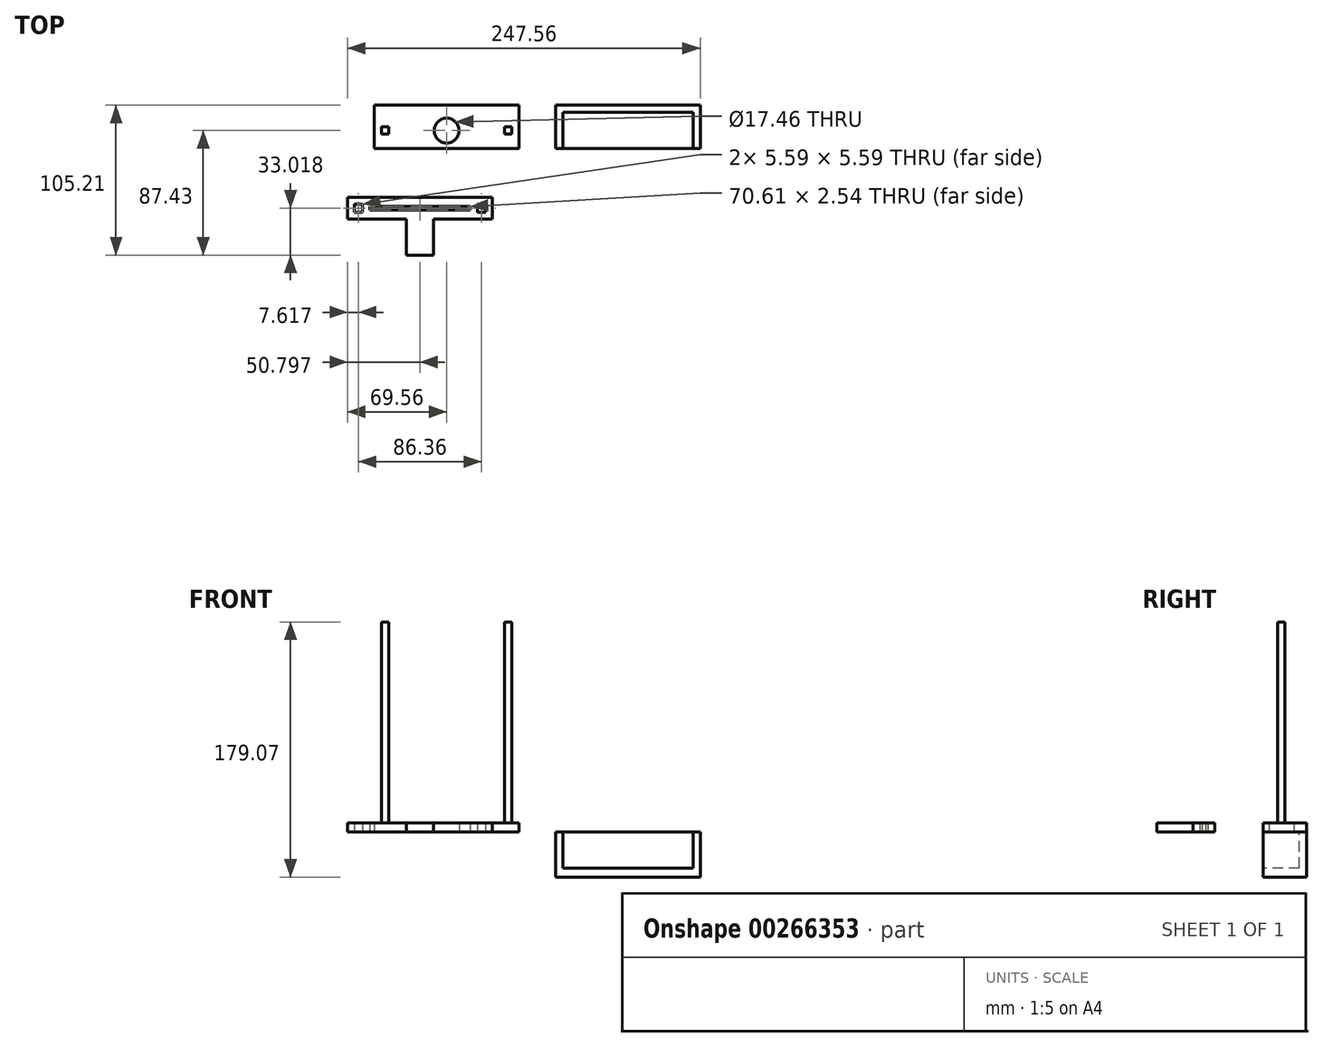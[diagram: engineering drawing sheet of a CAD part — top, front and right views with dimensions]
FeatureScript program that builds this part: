
annotation { "Feature Type Name" : "Feature", "Feature Type Description" : "" }
export const myFeature = defineFeature(function(context is Context, id is Id, definition is map)
    precondition{}
    {
        {
            var Q0;
            Q0=qCreatedBy(makeId("Top.planeOp"),FACE);
            var sketch = newSketch(context, id + "F0", { "sketchPlane" : qUnion([Q0])});
            skLineSegment(sketch, "E0.bottom", {"start": v(45.72, 12.7) * mm, "end": v(-45.72, 12.7) * mm});
            skLineSegment(sketch, "E0.top", {"start": v(50.8, -12.7) * mm, "end": v(-50.8, -12.7) * mm});
            skLineSegment(sketch, "E0.left", {"start": v(45.72, 12.7) * mm, "end": v(45.72, -12.7) * mm});
            skLineSegment(sketch, "E0.right", {"start": v(-45.72, 12.7) * mm, "end": v(-45.72, -12.7) * mm});
            skPoint(sketch, "E0.middle", {"position": v(0, 0) * mm});
            skCircle(sketch, "E1", {"center": v(0, 0) * mm, "radius": 8.73 * mm});
            skLineSegment(sketch, "E2.bottom", {"start": v(-45.72, 2.54) * mm, "end": v(-40.64, 2.54) * mm});
            skLineSegment(sketch, "E2.top", {"start": v(-45.72, -2.54) * mm, "end": v(-40.64, -2.54) * mm});
            skLineSegment(sketch, "E2.left", {"start": v(-45.72, 2.54) * mm, "end": v(-45.72, -2.54) * mm});
            skLineSegment(sketch, "E2.right", {"start": v(-40.64, 2.54) * mm, "end": v(-40.64, -2.54) * mm});
            skLineSegment(sketch, "E3.bottom", {"start": v(45.72, 2.54) * mm, "end": v(40.64, 2.54) * mm});
            skLineSegment(sketch, "E3.top", {"start": v(45.72, -2.54) * mm, "end": v(40.64, -2.54) * mm});
            skLineSegment(sketch, "E3.left", {"start": v(45.72, 2.54) * mm, "end": v(45.72, -2.54) * mm});
            skLineSegment(sketch, "E3.right", {"start": v(40.64, 2.54) * mm, "end": v(40.64, -2.54) * mm});
            skLineSegment(sketch, "E4", {"start": v(-40.64, 2.54) * mm, "end": v(40.64, 2.54) * mm, "construction": true});
            skLineSegment(sketch, "E5", {"start": v(-40.64, -2.54) * mm, "end": v(40.64, -2.54) * mm, "construction": true});
            skLineSegment(sketch, "E6", {"start": v(-45.72, 0) * mm, "end": v(45.72, 0) * mm, "construction": true});
            skPoint(sketch, "E7.orphan", {"position": v(-45.72, 12.7) * mm});
            skPoint(sketch, "E8.orphan", {"position": v(45.72, 12.7) * mm});
            skPoint(sketch, "E9.orphan", {"position": v(-45.72, -12.7) * mm});
            skPoint(sketch, "E10.orphan", {"position": v(45.72, -12.7) * mm});
            skLineSegment(sketch, "E11", {"start": v(-50.8, 17.78) * mm, "end": v(-50.8, -12.7) * mm});
            skLineSegment(sketch, "E12", {"start": v(-50.8, 17.78) * mm, "end": v(50.8, 17.78) * mm});
            skLineSegment(sketch, "E13", {"start": v(50.8, 17.78) * mm, "end": v(50.8, -12.7) * mm});
            skSolve(sketch);
        }
        {
            var Q0;
            Q0=makeQuery(id+"F0.imprint","IMPRINT",FACE,{"disambiguationData":[TD([[makeQuery(id+"F0.imprint","IMPRINT",EDGE,{"derivedFrom":sQuery(id+"F0.wireOp",EDGE,"E3.bottom")}),1.0]])]});
            var Q1;
            Q1=makeQuery(id+"F0.imprint","IMPRINT",FACE,{"disambiguationData":[TD([[makeQuery(id+"F0.imprint","IMPRINT",EDGE,{"derivedFrom":sQuery(id+"F0.wireOp",EDGE,"E2.bottom")}),-1.0]])]});
            extrude(context, id + "F1", {"entities" : qUnion([Q0, Q1]), "depth" : 147.32 * mm});
        }
        {
            var Q0;
            {var subQ5=sQuery(id+"F0.wireOp",EDGE,"E0.bottom");Q0=makeQuery(id+"F0.imprint","IMPRINT",FACE,{"disambiguationData":[TD([[makeQuery(id+"F0.imprint","IMPRINT",EDGE,{"derivedFrom":subQ5}),1.0]])]});}
            var Q1;
            {var subQ5=sQuery(id+"F0.wireOp",EDGE,"E0.bottom");Q1=makeQuery(id+"F0.imprint","IMPRINT",FACE,{"disambiguationData":[TD([[makeQuery(id+"F0.imprint","IMPRINT",EDGE,{"derivedFrom":subQ5}),-1.0]])]});}
            extrude(context, id + "F2", {"entities" : qUnion([Q0, Q1]), "operationType" : NewBodyOperationType.ADD, "depth" : 6.35 * mm});
        }
        {
            var Q0;
            Q0=qCreatedBy(makeId("Top.planeOp"),FACE);
            var sketch = newSketch(context, id + "F3", { "sketchPlane" : qUnion([Q0])});
            skLineSegment(sketch, "E14.left", {"start": v(-64.74, -51.62) * mm, "end": v(-64.74, -57.2) * mm});
            skLineSegment(sketch, "E14.right", {"start": v(27.21, -51.62) * mm, "end": v(27.21, -57.2) * mm});
            skLineSegment(sketch, "E15", {"start": v(-64.74, -51.62) * mm, "end": v(-59.15, -51.62) * mm});
            skLineSegment(sketch, "E16", {"start": v(27.21, -57.2) * mm, "end": v(21.62, -57.2) * mm});
            skLineSegment(sketch, "E17", {"start": v(-59.15, -51.62) * mm, "end": v(-59.15, -57.2) * mm});
            skLineSegment(sketch, "E18", {"start": v(21.62, -51.62) * mm, "end": v(21.62, -57.2) * mm});
            skLineSegment(sketch, "E19.trimOffspring", {"start": v(21.62, -51.62) * mm, "end": v(27.21, -51.62) * mm});
            skLineSegment(sketch, "E20.trimOffspring", {"start": v(-59.15, -57.2) * mm, "end": v(-64.74, -57.2) * mm});
            skLineSegment(sketch, "E21", {"start": v(-59.15, -51.62) * mm, "end": v(-54.07, -51.62) * mm});
            skLineSegment(sketch, "E22", {"start": v(21.62, -57.2) * mm, "end": v(16.54, -57.2) * mm});
            skLineSegment(sketch, "E23", {"start": v(-64.74, -54.41) * mm, "end": v(27.21, -54.41) * mm, "construction": true});
            skPoint(sketch, "E24", {"position": v(-59.15, -54.41) * mm});
            skPoint(sketch, "E25", {"position": v(21.62, -54.41) * mm});
            skLineSegment(sketch, "E26", {"start": v(-69.56, -62.03) * mm, "end": v(-69.56, -46.8) * mm});
            skLineSegment(sketch, "E27", {"start": v(-69.56, -46.8) * mm, "end": v(32.04, -46.8) * mm});
            skLineSegment(sketch, "E28", {"start": v(32.04, -46.8) * mm, "end": v(32.04, -62.03) * mm});
            skLineSegment(sketch, "E29", {"start": v(-69.56, -62.03) * mm, "end": v(32.04, -62.03) * mm});
            skLineSegment(sketch, "E30", {"start": v(-54.07, -51.62) * mm, "end": v(-54.07, -57.2) * mm});
            skLineSegment(sketch, "E31", {"start": v(16.54, -51.62) * mm, "end": v(16.54, -57.2) * mm});
            skLineSegment(sketch, "E32.trimOffspring", {"start": v(16.54, -51.62) * mm, "end": v(21.62, -51.62) * mm});
            skLineSegment(sketch, "E33.trimOffspring", {"start": v(-54.07, -57.2) * mm, "end": v(-59.15, -57.2) * mm});
            skLineSegment(sketch, "E34", {"start": v(-54.07, -53.14) * mm, "end": v(16.54, -53.14) * mm});
            skLineSegment(sketch, "E35", {"start": v(-54.07, -55.68) * mm, "end": v(16.54, -55.68) * mm});
            skPoint(sketch, "E36", {"position": v(-54.07, -54.41) * mm});
            skPoint(sketch, "E37", {"position": v(16.54, -54.41) * mm});
            skLineSegment(sketch, "E38", {"start": v(27.21, -57.2) * mm, "end": v(27.21, -62.03) * mm, "construction": true});
            skLineSegment(sketch, "E39", {"start": v(27.21, -51.62) * mm, "end": v(32.04, -51.62) * mm, "construction": true});
            skLineSegment(sketch, "E40", {"start": v(-64.74, -51.62) * mm, "end": v(-64.74, -46.8) * mm, "construction": true});
            skLineSegment(sketch, "E41", {"start": v(-64.74, -57.2) * mm, "end": v(-69.56, -57.2) * mm, "construction": true});
            skLineSegment(sketch, "E42", {"start": v(-28.29, -62.03) * mm, "end": v(-28.29, -87.43) * mm});
            skLineSegment(sketch, "E43", {"start": v(-28.29, -87.43) * mm, "end": v(-9.24, -87.43) * mm});
            skLineSegment(sketch, "E44", {"start": v(-9.24, -87.43) * mm, "end": v(-9.24, -62.03) * mm});
            skPoint(sketch, "E44.endSnap0", {"position": v(-18.76, -62.03) * mm});
            skLineSegment(sketch, "E45", {"start": v(-18.76, -62.03) * mm, "end": v(-18.76, -87.43) * mm, "construction": true});
            skSolve(sketch);
        }
        {
            var Q0;
            {var subQ0=sQuery(id+"F3.wireOp",EDGE,"E18");Q0=makeQuery(id+"F3.imprint","IMPRINT",FACE,{"disambiguationData":[TD([[makeQuery(id+"F3.imprint","IMPRINT",EDGE,{"derivedFrom":subQ0}),-1.0]])]});}
            var Q1;
            Q1=makeQuery(id+"F3.imprint","IMPRINT",FACE,{"disambiguationData":[TD([[makeQuery(id+"F3.imprint","IMPRINT",EDGE,{"derivedFrom":sQuery(id+"F3.wireOp",EDGE,"E14.left")}),-1.0]])]});
            var Q2;
            {var subQ0=sQuery(id+"F3.wireOp",EDGE,"E17");Q2=makeQuery(id+"F3.imprint","IMPRINT",FACE,{"disambiguationData":[TD([[makeQuery(id+"F3.imprint","IMPRINT",EDGE,{"derivedFrom":subQ0}),1.0]])]});}
            var Q3;
            {var subQ0=sQuery(id+"F3.wireOp",EDGE,"E42");Q3=makeQuery(id+"F3.imprint","IMPRINT",FACE,{"disambiguationData":[TD([[makeQuery(id+"F3.imprint","IMPRINT",EDGE,{"derivedFrom":subQ0}),1.0]])]});}
            extrude(context, id + "F4", {"entities" : qUnion([Q0, Q1, Q2, Q3]), "depth" : 6.35 * mm});
        }
        {
            var Q0;
            Q0=qCreatedBy(makeId("Top.planeOp"),FACE);
            var sketch = newSketch(context, id + "F5", { "sketchPlane" : qUnion([Q0])});
            skLineSegment(sketch, "E46.bottom", {"start": v(172.92, 12.7) * mm, "end": v(81.48, 12.7) * mm});
            skLineSegment(sketch, "E46.top", {"start": v(178, -12.7) * mm, "end": v(76.4, -12.7) * mm});
            skLineSegment(sketch, "E46.left", {"start": v(172.92, 12.7) * mm, "end": v(172.92, -12.7) * mm});
            skLineSegment(sketch, "E46.right", {"start": v(81.48, 12.7) * mm, "end": v(81.48, -12.7) * mm});
            skLineSegment(sketch, "E47.bottom", {"start": v(81.48, 2.54) * mm, "end": v(86.56, 2.54) * mm});
            skLineSegment(sketch, "E47.top", {"start": v(81.48, -2.54) * mm, "end": v(86.56, -2.54) * mm});
            skLineSegment(sketch, "E47.left", {"start": v(81.48, 2.54) * mm, "end": v(81.48, -2.54) * mm});
            skLineSegment(sketch, "E47.right", {"start": v(86.56, 2.54) * mm, "end": v(86.56, -2.54) * mm});
            skLineSegment(sketch, "E48.bottom", {"start": v(172.92, 2.54) * mm, "end": v(167.84, 2.54) * mm});
            skLineSegment(sketch, "E48.top", {"start": v(172.92, -2.54) * mm, "end": v(167.84, -2.54) * mm});
            skLineSegment(sketch, "E48.left", {"start": v(172.92, 2.54) * mm, "end": v(172.92, -2.54) * mm});
            skLineSegment(sketch, "E48.right", {"start": v(167.84, 2.54) * mm, "end": v(167.84, -2.54) * mm});
            skLineSegment(sketch, "E49", {"start": v(86.56, 2.54) * mm, "end": v(167.84, 2.54) * mm, "construction": true});
            skLineSegment(sketch, "E50", {"start": v(86.56, -2.54) * mm, "end": v(167.84, -2.54) * mm, "construction": true});
            skLineSegment(sketch, "E51", {"start": v(81.48, 0) * mm, "end": v(172.92, 0) * mm, "construction": true});
            skPoint(sketch, "E52.orphan", {"position": v(81.48, 12.7) * mm});
            skPoint(sketch, "E53.orphan", {"position": v(172.92, 12.7) * mm});
            skPoint(sketch, "E54.orphan", {"position": v(81.48, -12.7) * mm});
            skPoint(sketch, "E55.orphan", {"position": v(172.92, -12.7) * mm});
            skLineSegment(sketch, "E56", {"start": v(76.4, 17.78) * mm, "end": v(76.4, -12.7) * mm});
            skLineSegment(sketch, "E57", {"start": v(76.4, 17.78) * mm, "end": v(178, 17.78) * mm});
            skLineSegment(sketch, "E58", {"start": v(178, 17.78) * mm, "end": v(178, -12.7) * mm});
            skSolve(sketch);
        }
        {
            var Q0;
            Q0=makeQuery(id+"F5.imprint","IMPRINT",FACE,{"disambiguationData":[TD([[makeQuery(id+"F5.imprint","IMPRINT",EDGE,{"derivedFrom":sQuery(id+"F5.wireOp",EDGE,"86bbf15a-d8a8-4ceb-aa72-a7a4e9ccc14b")}),1.0]])]});
            var Q1;
            {var subQ2=sQuery(id+"F5.wireOp",EDGE,"E46.bottom");Q1=makeQuery(id+"F5.imprint","IMPRINT",FACE,{"disambiguationData":[TD([[makeQuery(id+"F5.imprint","IMPRINT",EDGE,{"derivedFrom":subQ2}),1.0]])]});}
            var Q2;
            {var subQ6=sQuery(id+"F5.wireOp",EDGE,"E46.bottom");Q2=makeQuery(id+"F5.imprint","IMPRINT",FACE,{"disambiguationData":[TD([[makeQuery(id+"F5.imprint","IMPRINT",EDGE,{"derivedFrom":subQ6}),-1.0]])]});}
            var Q3;
            Q3=makeQuery(id+"F5.imprint","IMPRINT",FACE,{"disambiguationData":[TD([[makeQuery(id+"F5.imprint","IMPRINT",EDGE,{"derivedFrom":sQuery(id+"F5.wireOp",EDGE,"E47.bottom")}),-1.0]])]});
            var Q4;
            Q4=makeQuery(id+"F5.imprint","IMPRINT",FACE,{"disambiguationData":[TD([[makeQuery(id+"F5.imprint","IMPRINT",EDGE,{"derivedFrom":sQuery(id+"F5.wireOp",EDGE,"E48.bottom")}),1.0]])]});
            extrude(context, id + "F6", {"entities" : qUnion([Q0, Q1, Q2, Q3, Q4]), "operationType" : NewBodyOperationType.ADD, "oppositeDirection" : true, "depth" : 31.75 * mm});
        }
        {
            var Q0;
            {var subQ6=sQuery(id+"F5.wireOp",EDGE,"E46.bottom");Q0=makeQuery(id+"F5.imprint","IMPRINT",FACE,{"disambiguationData":[TD([[makeQuery(id+"F5.imprint","IMPRINT",EDGE,{"derivedFrom":subQ6}),1.0]])]});}
            var Q1;
            Q1=makeQuery(id+"F5.imprint","IMPRINT",FACE,{"disambiguationData":[TD([[makeQuery(id+"F5.imprint","IMPRINT",EDGE,{"derivedFrom":sQuery(id+"F5.wireOp",EDGE,"86bbf15a-d8a8-4ceb-aa72-a7a4e9ccc14b")}),1.0]])]});
            var Q2;
            Q2=makeQuery(id+"F5.imprint","IMPRINT",FACE,{"disambiguationData":[TD([[makeQuery(id+"F5.imprint","IMPRINT",EDGE,{"derivedFrom":sQuery(id+"F5.wireOp",EDGE,"E48.bottom")}),1.0]])]});
            var Q3;
            Q3=makeQuery(id+"F5.imprint","IMPRINT",FACE,{"disambiguationData":[TD([[makeQuery(id+"F5.imprint","IMPRINT",EDGE,{"derivedFrom":sQuery(id+"F5.wireOp",EDGE,"E47.bottom")}),-1.0]])]});
            extrude(context, id + "F7", {"entities" : qUnion([Q0, Q1, Q2, Q3]), "operationType" : NewBodyOperationType.REMOVE, "oppositeDirection" : true, "depth" : 25.4 * mm});
        }
    });
